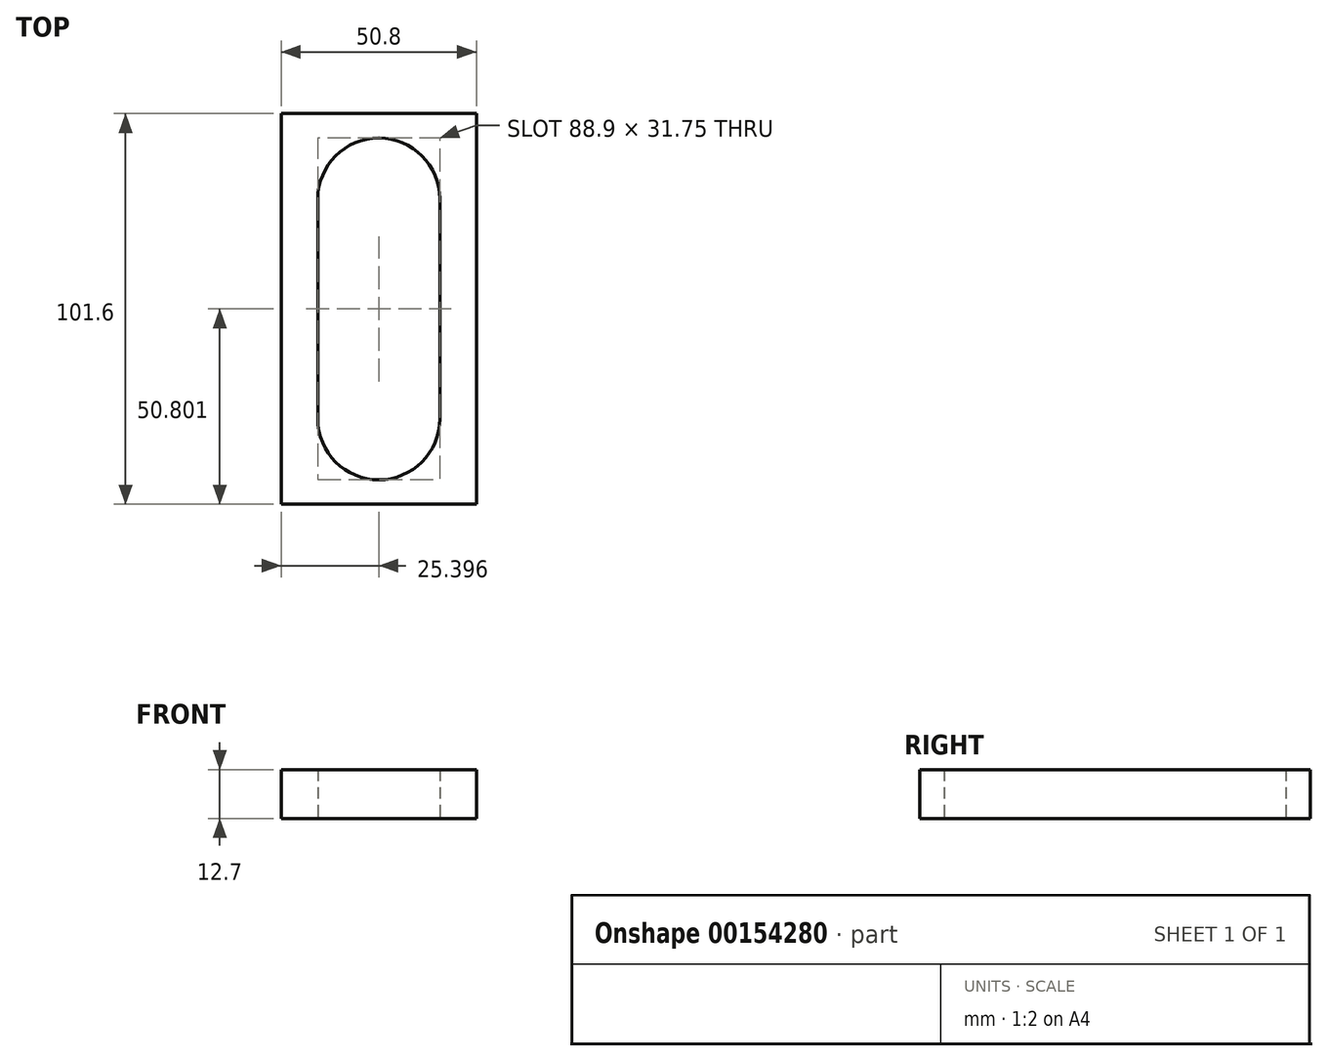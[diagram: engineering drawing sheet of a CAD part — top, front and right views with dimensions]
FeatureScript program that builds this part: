
annotation { "Feature Type Name" : "Feature", "Feature Type Description" : "" }
export const myFeature = defineFeature(function(context is Context, id is Id, definition is map)
    precondition{}
    {
        {
            var Q0;
            Q0=qCreatedBy(makeId("Top.planeOp"),FACE);
            var sketch = newSketch(context, id + "F0", { "sketchPlane" : qUnion([Q0])});
            skLineSegment(sketch, "E0.bottom", {"start": v(-27.48, 60.36) * mm, "end": v(23.32, 60.36) * mm});
            skLineSegment(sketch, "E0.top", {"start": v(-27.48, -41.24) * mm, "end": v(23.32, -41.24) * mm});
            skLineSegment(sketch, "E0.left", {"start": v(-27.48, 60.36) * mm, "end": v(-27.48, -41.24) * mm});
            skLineSegment(sketch, "E0.right", {"start": v(23.32, 60.36) * mm, "end": v(23.32, -41.24) * mm});
            skLineSegment(sketch, "E1", {"start": v(-27.48, 60.36) * mm, "end": v(-17.96, 60.36) * mm, "construction": true});
            skLineSegment(sketch, "E2", {"start": v(23.32, 60.36) * mm, "end": v(13.8, 60.36) * mm, "construction": true});
            skLineSegment(sketch, "E3", {"start": v(23.32, 60.36) * mm, "end": v(23.32, 54.01) * mm, "construction": true});
            skLineSegment(sketch, "E4", {"start": v(23.32, -41.24) * mm, "end": v(23.32, -34.89) * mm, "construction": true});
            skLineSegment(sketch, "E5", {"start": v(-17.96, 60.36) * mm, "end": v(-17.96, -41.24) * mm, "construction": true});
            skLineSegment(sketch, "E6", {"start": v(23.32, -34.89) * mm, "end": v(-27.48, -34.89) * mm, "construction": true});
            skLineSegment(sketch, "E7", {"start": v(23.32, 54.01) * mm, "end": v(-27.48, 54.01) * mm, "construction": true});
            skLineSegment(sketch, "E8", {"start": v(13.8, -34.89) * mm, "end": v(13.8, -19.01) * mm, "construction": true});
            skLineSegment(sketch, "E9", {"start": v(-17.96, 38.14) * mm, "end": v(-17.96, -19.01) * mm, "construction": true});
            skArc(sketch, "E10", {"start": v(-17.96, 38.14) * mm, "mid": v(-2.08, 54.01) * mm, "end": v(13.8, 38.14) * mm});
            skArc(sketch, "E11", {"start": v(-17.96, -19.01) * mm, "mid": v(-2.08, -34.89) * mm, "end": v(13.8, -19.01) * mm});
            skLineSegment(sketch, "E12", {"start": v(-2.08, 54.01) * mm, "end": v(-2.08, 42.9) * mm, "construction": true});
            skLineSegment(sketch, "E13", {"start": v(-2.08, -34.89) * mm, "end": v(-2.08, -4.71) * mm, "construction": true});
            skCircle(sketch, "E14", {"center": v(-2.08, -4.71) * mm, "radius": 2.12 * mm});
            skCircle(sketch, "E15", {"center": v(-2.08, 42.9) * mm, "radius": 2.12 * mm});
            skLineSegment(sketch, "E16", {"start": v(-17.96, 38.14) * mm, "end": v(-10.02, 38.14) * mm, "construction": true});
            skLineSegment(sketch, "E17", {"start": v(13.8, 38.14) * mm, "end": v(5.85, 38.14) * mm, "construction": true});
            skLineSegment(sketch, "E18.bottom", {"start": v(-10.02, 38.14) * mm, "end": v(-6.85, 38.14) * mm});
            skLineSegment(sketch, "E18.top", {"start": v(-10.02, 28.61) * mm, "end": v(-6.85, 28.61) * mm});
            skLineSegment(sketch, "E18.left", {"start": v(-10.02, 38.14) * mm, "end": v(-10.02, 28.61) * mm});
            skLineSegment(sketch, "E18.right", {"start": v(-6.85, 38.14) * mm, "end": v(-6.85, 28.61) * mm});
            skLineSegment(sketch, "E19.bottom", {"start": v(5.85, 38.14) * mm, "end": v(2.68, 38.14) * mm});
            skLineSegment(sketch, "E19.top", {"start": v(5.85, 28.61) * mm, "end": v(2.68, 28.61) * mm});
            skLineSegment(sketch, "E19.left", {"start": v(5.85, 38.14) * mm, "end": v(5.85, 28.61) * mm});
            skLineSegment(sketch, "E19.right", {"start": v(2.68, 38.14) * mm, "end": v(2.68, 28.61) * mm});
            skLineSegment(sketch, "E20", {"start": v(-17.96, -19.01) * mm, "end": v(-10.02, -19.01) * mm, "construction": true});
            skLineSegment(sketch, "E21", {"start": v(13.8, -19.01) * mm, "end": v(5.85, -19.01) * mm, "construction": true});
            skLineSegment(sketch, "E22.bottom", {"start": v(-10.02, -19.01) * mm, "end": v(-6.85, -19.01) * mm});
            skLineSegment(sketch, "E22.top", {"start": v(-10.02, -9.49) * mm, "end": v(-6.85, -9.49) * mm});
            skLineSegment(sketch, "E22.left", {"start": v(-10.02, -19.01) * mm, "end": v(-10.02, -9.49) * mm});
            skLineSegment(sketch, "E22.right", {"start": v(-6.85, -19.01) * mm, "end": v(-6.85, -9.49) * mm});
            skLineSegment(sketch, "E23.bottom", {"start": v(5.85, -19.01) * mm, "end": v(2.68, -19.01) * mm});
            skLineSegment(sketch, "E23.top", {"start": v(5.85, -9.49) * mm, "end": v(2.68, -9.49) * mm});
            skLineSegment(sketch, "E23.left", {"start": v(5.85, -19.01) * mm, "end": v(5.85, -9.49) * mm});
            skLineSegment(sketch, "E23.right", {"start": v(2.68, -19.01) * mm, "end": v(2.68, -9.49) * mm});
            skLineSegment(sketch, "E24", {"start": v(-17.96, 38.14) * mm, "end": v(-17.96, -19.01) * mm});
            skLineSegment(sketch, "E25", {"start": v(13.8, 38.14) * mm, "end": v(13.8, -19.01) * mm});
            skLineSegment(sketch, "E26", {"start": v(-6.85, 38.14) * mm, "end": v(2.68, 38.14) * mm, "construction": true});
            skLineSegment(sketch, "E27", {"start": v(-6.85, -9.49) * mm, "end": v(2.68, -9.49) * mm, "construction": true});
            skSolve(sketch);
        }
        {
            var Q0;
            Q0=makeQuery(id+"F0.imprint","IMPRINT",FACE,{"disambiguationData":[TD([[makeQuery(id+"F0.imprint","IMPRINT",EDGE,{"derivedFrom":sQuery(id+"F0.wireOp",EDGE,"E0.bottom")}),-1.0]])]});
            var Q1;
            Q1=makeQuery(id+"F0.imprint","IMPRINT",FACE,{"disambiguationData":[TD([[makeQuery(id+"F0.imprint","IMPRINT",EDGE,{"derivedFrom":sQuery(id+"F0.wireOp",EDGE,"E10")}),-1.0]])]});
            extrude(context, id + "F1", {"entities" : qUnion([Q0, Q1]), "depth" : 6.35 * mm});
        }
        {
            var Q0;
            Q0=makeQuery(id+"F0.imprint","IMPRINT",FACE,{"disambiguationData":[TD([[makeQuery(id+"F0.imprint","IMPRINT",EDGE,{"derivedFrom":sQuery(id+"F0.wireOp",EDGE,"E10")}),-1.0]])]});
            extrude(context, id + "F2", {"entities" : qUnion([Q0]), "operationType" : NewBodyOperationType.ADD, "depth" : 12.7 * mm});
        }
    });
